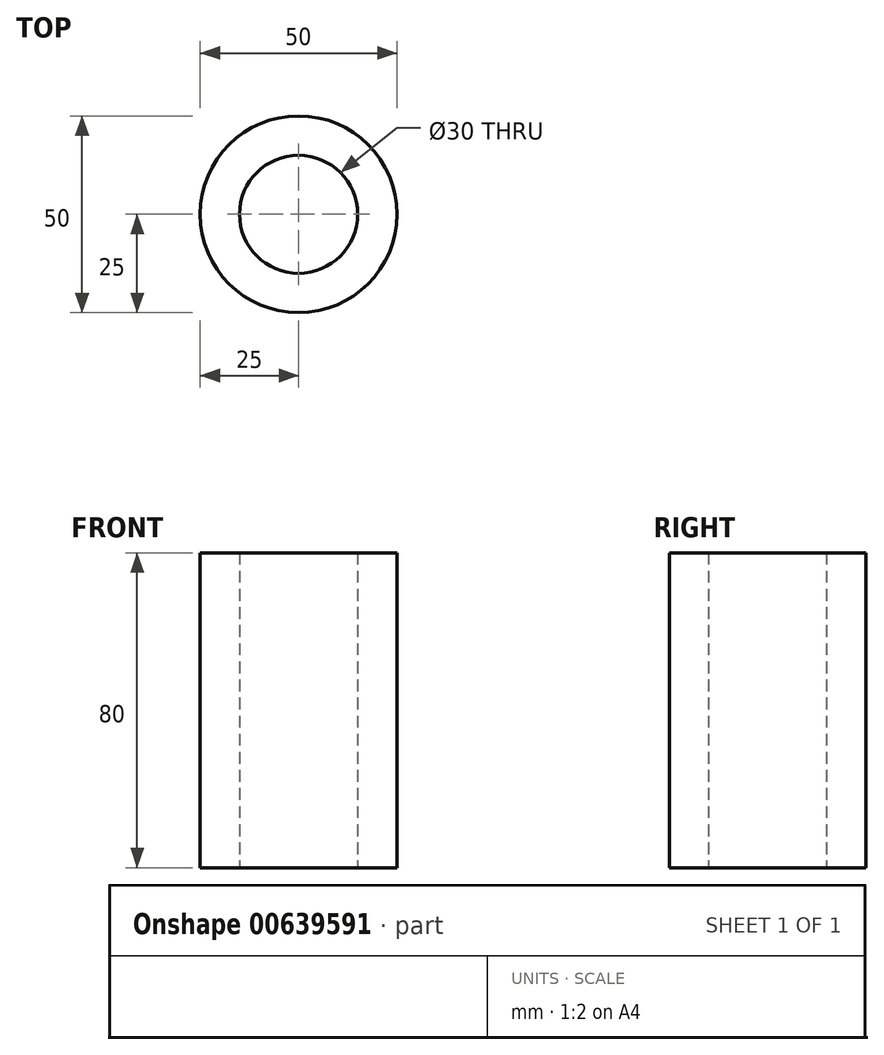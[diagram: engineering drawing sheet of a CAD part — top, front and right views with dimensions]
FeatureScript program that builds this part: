
annotation { "Feature Type Name" : "Feature", "Feature Type Description" : "" }
export const myFeature = defineFeature(function(context is Context, id is Id, definition is map)
    precondition{}
    {
        {
            var Q0;
            Q0=qCreatedBy(makeId("Top.planeOp"),FACE);
            var sketch = newSketch(context, id + "F0", { "sketchPlane" : qUnion([Q0])});
            skCircle(sketch, "E0", {"center": v(0, 0) * mm, "radius": 15 * mm});
            skCircle(sketch, "E1", {"center": v(0, 0) * mm, "radius": 25 * mm});
            skSolve(sketch);
        }
        {
            var Q0;
            Q0 = qSketchRegion(id + "F0", true);
            extrude(context, id + "F1", {"entities" : qUnion([Q0]), "depth" : 80 * mm, "offsetDistance" : 25 * mm});
        }
    });
